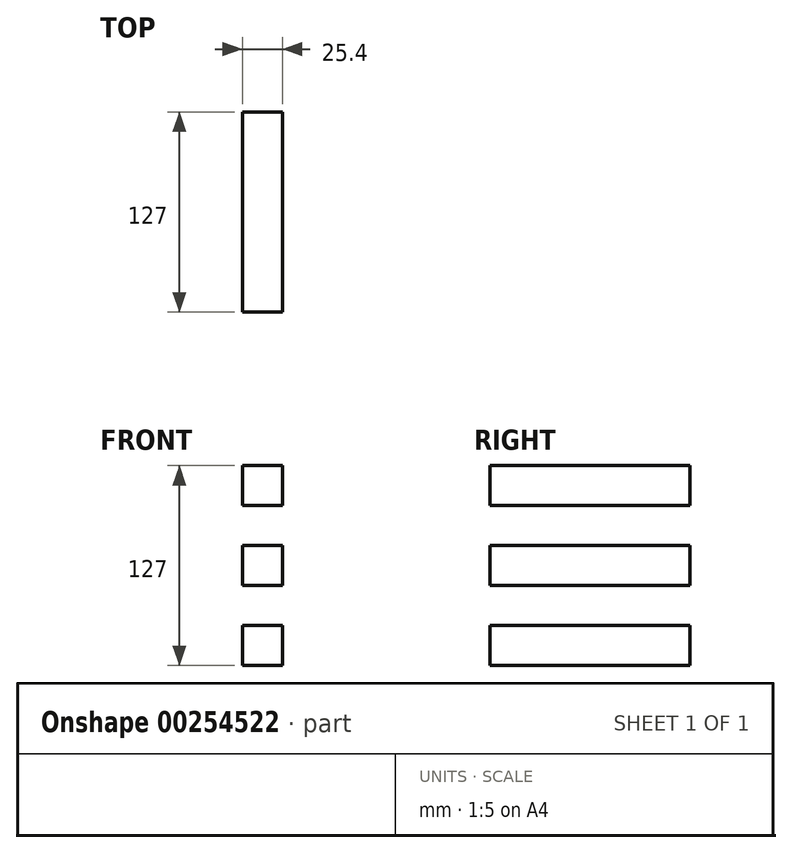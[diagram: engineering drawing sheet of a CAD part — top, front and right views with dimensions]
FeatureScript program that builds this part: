
annotation { "Feature Type Name" : "Feature", "Feature Type Description" : "" }
export const myFeature = defineFeature(function(context is Context, id is Id, definition is map)
    precondition{}
    {
        {
            var Q0;
            Q0=qCreatedBy(makeId("Front.planeOp"),FACE);
            var sketch = newSketch(context, id + "F0", { "sketchPlane" : qUnion([Q0])});
            skLineSegment(sketch, "E0.bottom", {"start": v(12.7, 12.7) * mm, "end": v(-12.7, 12.7) * mm});
            skLineSegment(sketch, "E0.top", {"start": v(12.7, -12.7) * mm, "end": v(-12.7, -12.7) * mm});
            skLineSegment(sketch, "E0.left", {"start": v(12.7, 12.7) * mm, "end": v(12.7, -12.7) * mm});
            skLineSegment(sketch, "E0.right", {"start": v(-12.7, 12.7) * mm, "end": v(-12.7, -12.7) * mm});
            skPoint(sketch, "E0.middle", {"position": v(0, 0) * mm});
            skLineSegment(sketch, "E1", {"start": v(0, 0) * mm, "end": v(0, 50.8) * mm});
            skPoint(sketch, "E1.endSnap0", {"position": v(0, 12.7) * mm});
            skLineSegment(sketch, "E2", {"start": v(0, 0) * mm, "end": v(0, -50.8) * mm});
            skPoint(sketch, "E2.endSnap0", {"position": v(0, -12.7) * mm});
            skLineSegment(sketch, "E3.bottom", {"start": v(12.7, 63.5) * mm, "end": v(-12.7, 63.5) * mm});
            skLineSegment(sketch, "E3.top", {"start": v(12.7, 38.1) * mm, "end": v(-12.7, 38.1) * mm});
            skLineSegment(sketch, "E3.left", {"start": v(12.7, 63.5) * mm, "end": v(12.7, 38.1) * mm});
            skLineSegment(sketch, "E3.right", {"start": v(-12.7, 63.5) * mm, "end": v(-12.7, 38.1) * mm});
            skPoint(sketch, "E3.middle", {"position": v(0, 50.8) * mm});
            skLineSegment(sketch, "E4.bottom", {"start": v(12.7, -38.1) * mm, "end": v(-12.7, -38.1) * mm});
            skLineSegment(sketch, "E4.top", {"start": v(12.7, -63.5) * mm, "end": v(-12.7, -63.5) * mm});
            skLineSegment(sketch, "E4.left", {"start": v(12.7, -38.1) * mm, "end": v(12.7, -63.5) * mm});
            skLineSegment(sketch, "E4.right", {"start": v(-12.7, -38.1) * mm, "end": v(-12.7, -63.5) * mm});
            skPoint(sketch, "E4.middle", {"position": v(0, -50.8) * mm});
            skSolve(sketch);
        }
        {
            var Q0;
            Q0 = qSketchRegion(id + "F0", true);
            extrude(context, id + "F1", {"entities" : qUnion([Q0]), "endBound" : BoundingType.SYMMETRIC, "depth" : 127 * mm});
        }
    });
